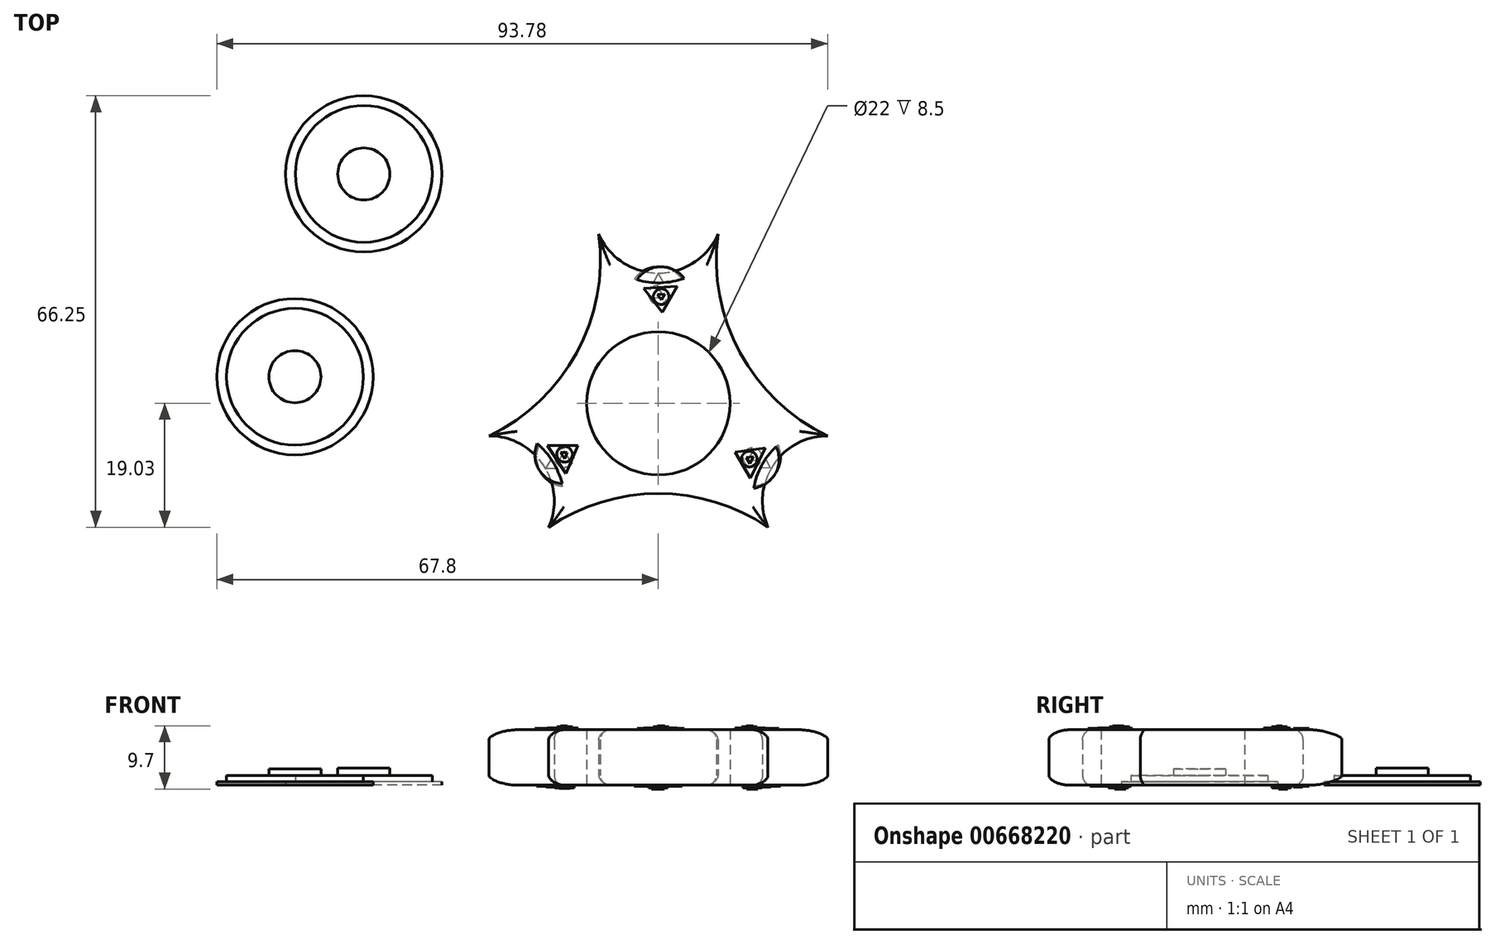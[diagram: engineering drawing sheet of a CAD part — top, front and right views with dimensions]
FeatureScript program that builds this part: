
annotation { "Feature Type Name" : "Feature", "Feature Type Description" : "" }
export const myFeature = defineFeature(function(context is Context, id is Id, definition is map)
    precondition{}
    {
        {
            var Q0;
            Q0=qCreatedBy(makeId("Top.planeOp"),FACE);
            var sketch = newSketch(context, id + "F0", { "sketchPlane" : qUnion([Q0])});
            skCircle(sketch, "E0", {"center": v(0, 0) * mm, "radius": 11 * mm});
            skLineSegment(sketch, "E1", {"start": v(0, 30) * mm, "end": v(0, 0) * mm});
            skLineSegment(sketch, "E2.0", {"start": v(-25.98, 15) * mm, "end": v(25.98, 15) * mm});
            skLineSegment(sketch, "E2.1", {"start": v(25.98, 15) * mm, "end": v(0, -30) * mm});
            skLineSegment(sketch, "E2.2", {"start": v(0, -30) * mm, "end": v(-25.98, 15) * mm});
            skPoint(sketch, "E2.0.midPoint", {"position": v(0, 15) * mm});
            skLineSegment(sketch, "E3", {"start": v(0, 0) * mm, "end": v(25.98, -15) * mm});
            skLineSegment(sketch, "E4", {"start": v(25.98, -15) * mm, "end": v(0, 0) * mm});
            skLineSegment(sketch, "E5", {"start": v(0, 0) * mm, "end": v(-25.98, -15) * mm});
            skLineSegment(sketch, "E6", {"start": v(-25.98, -15) * mm, "end": v(0, 0) * mm});
            skCircle(sketch, "E7", {"center": v(-25.98, -15) * mm, "radius": 10 * mm});
            skCircle(sketch, "E8", {"center": v(25.98, -15) * mm, "radius": 10 * mm});
            skCircle(sketch, "E9", {"center": v(0, 30) * mm, "radius": 10 * mm});
            skArc(sketch, "E10", {"start": v(16.83, -19.02) * mm, "mid": v(0, -13.86) * mm, "end": v(-16.83, -19.03) * mm});
            skArc(sketch, "E11", {"start": v(-25.98, -5) * mm, "mid": v(-12.54, 7.76) * mm, "end": v(-9.15, 25.97) * mm});
            skArc(sketch, "E12", {"start": v(9.15, 25.97) * mm, "mid": v(12.54, 7.76) * mm, "end": v(25.98, -5) * mm});
            skPoint(sketch, "E13.0.midPoint", {"position": v(18.83, -15) * mm});
            skPoint(sketch, "E14.0.midPoint", {"position": v(-18.83, -15) * mm});
            skPoint(sketch, "E15.0.midPoint", {"position": v(7.15, 30) * mm});
            skPoint(sketch, "E16.orphan", {"position": v(7.15, 34.13) * mm});
            skPoint(sketch, "E15.1.start.orphan", {"position": v(7.15, 25.87) * mm});
            skPoint(sketch, "E13.0.end.orphan", {"position": v(18.83, -10.87) * mm});
            skPoint(sketch, "E13.5.end.orphan", {"position": v(18.83, -19.13) * mm});
            skPoint(sketch, "E17.orphan", {"position": v(-18.83, -10.87) * mm});
            skPoint(sketch, "E14.0.end.orphan", {"position": v(-18.83, -19.13) * mm});
            skCircle(sketch, "E18.cCircle", {"center": v(0, 30) * mm, "radius": 7.02 * mm, "construction": true});
            skLineSegment(sketch, "E18.0", {"start": v(0, 37.02) * mm, "end": v(6.08, 33.51) * mm});
            skLineSegment(sketch, "E18.1", {"start": v(6.08, 33.51) * mm, "end": v(6.08, 26.49) * mm});
            skLineSegment(sketch, "E18.2", {"start": v(6.08, 26.49) * mm, "end": v(0, 22.98) * mm});
            skLineSegment(sketch, "E18.3", {"start": v(0, 22.98) * mm, "end": v(-6.08, 26.49) * mm});
            skLineSegment(sketch, "E18.4", {"start": v(-6.08, 26.49) * mm, "end": v(-6.08, 33.51) * mm});
            skLineSegment(sketch, "E18.5", {"start": v(-6.08, 33.51) * mm, "end": v(0, 37.02) * mm});
            skSolve(sketch);
        }
        {
            var Q0;
            Q0=makeQuery(id+"F0.imprint","IMPRINT",FACE,{"disambiguationData":[TD([[makeQuery(id+"F0.imprint","IMPRINT",EDGE,{"derivedFrom":sQuery(id+"F0.wireOp",EDGE,"E15.0")}),1.0]])]});
            var Q1;
            {var subQ0=sQuery(id+"F0.wireOp",EDGE,"E9");var subQ1=sQuery(id+"F0.wireOp",EDGE,"E1");var subQ2=makeQuery(id+"F0.imprint","INTERSECT",VERTEX,{"derivedFrom":[subQ1,subQ0]});Q1=makeQuery(id+"F0.imprint","IMPRINT",FACE,{"disambiguationData":[TD([[makeQuery(id+"F0.imprint","IMPRINT",EDGE,{"disambiguationData":[TD([[subQ2,-1.0]])],"derivedFrom":subQ1}),-1.0]])]});}
            var Q2;
            {var subQ0=sQuery(id+"F0.wireOp",EDGE,"E9");var subQ1=sQuery(id+"F0.wireOp",EDGE,"E1");var subQ2=makeQuery(id+"F0.imprint","INTERSECT",VERTEX,{"derivedFrom":[subQ1,subQ0]});Q2=makeQuery(id+"F0.imprint","IMPRINT",FACE,{"disambiguationData":[TD([[makeQuery(id+"F0.imprint","IMPRINT",EDGE,{"disambiguationData":[TD([[subQ2,-1.0]])],"derivedFrom":subQ1}),1.0]])]});}
            var Q3;
            {var subQ7=sQuery(id+"F0.wireOp",EDGE,"E1");var subQ9=sQuery(id+"F0.wireOp",EDGE,"E0");var subQ11=makeQuery(id+"F0.imprint","INTERSECT",VERTEX,{"derivedFrom":[subQ9,subQ7]});Q3=makeQuery(id+"F0.imprint","IMPRINT",FACE,{"disambiguationData":[TD([[makeQuery(id+"F0.imprint","IMPRINT",EDGE,{"disambiguationData":[TD([[subQ11,1.0]])],"derivedFrom":subQ9}),-1.0]])]});}
            var Q4;
            {var subQ3=sQuery(id+"F0.wireOp",EDGE,"E6");var subQ9=sQuery(id+"F0.wireOp",EDGE,"E0");var subQ11=makeQuery(id+"F0.imprint","INTERSECT",VERTEX,{"derivedFrom":[subQ9,subQ3]});Q4=makeQuery(id+"F0.imprint","IMPRINT",FACE,{"disambiguationData":[TD([[makeQuery(id+"F0.imprint","IMPRINT",EDGE,{"disambiguationData":[TD([[subQ11,1.0]])],"derivedFrom":subQ9}),-1.0]])]});}
            var Q5;
            Q5=makeQuery(id+"F0.imprint","IMPRINT",FACE,{"disambiguationData":[TD([[makeQuery(id+"F0.imprint","IMPRINT",EDGE,{"derivedFrom":sQuery(id+"F0.wireOp",EDGE,"E14.0")}),1.0]])]});
            var Q6;
            {var subQ0=sQuery(id+"F0.wireOp",EDGE,"E11");var subQ1=sQuery(id+"F0.wireOp",EDGE,"E2.2");var subQ2=makeQuery(id+"F0.imprint","INTERSECT",VERTEX,{"derivedFrom":[subQ1,subQ0]});Q6=makeQuery(id+"F0.imprint","IMPRINT",FACE,{"disambiguationData":[TD([[makeQuery(id+"F0.imprint","IMPRINT",EDGE,{"disambiguationData":[TD([[subQ2,1.0]])],"derivedFrom":subQ1}),1.0]])]});}
            var Q7;
            {var subQ0=sQuery(id+"F0.wireOp",EDGE,"E10");var subQ1=sQuery(id+"F0.wireOp",EDGE,"E2.2");var subQ2=makeQuery(id+"F0.imprint","INTERSECT",VERTEX,{"derivedFrom":[subQ1,subQ0]});Q7=makeQuery(id+"F0.imprint","IMPRINT",FACE,{"disambiguationData":[TD([[makeQuery(id+"F0.imprint","IMPRINT",EDGE,{"disambiguationData":[TD([[subQ2,-1.0]])],"derivedFrom":subQ1}),1.0]])]});}
            var Q8;
            {var subQ1=sQuery(id+"F0.wireOp",EDGE,"E0");var subQ8=sQuery(id+"F0.wireOp",EDGE,"E6");var subQ11=makeQuery(id+"F0.imprint","INTERSECT",VERTEX,{"derivedFrom":[subQ1,subQ8]});Q8=makeQuery(id+"F0.imprint","IMPRINT",FACE,{"disambiguationData":[TD([[makeQuery(id+"F0.imprint","IMPRINT",EDGE,{"disambiguationData":[TD([[subQ11,-1.0]])],"derivedFrom":subQ1}),-1.0]])]});}
            var Q9;
            {var subQ0=sQuery(id+"F0.wireOp",EDGE,"E10");var subQ1=sQuery(id+"F0.wireOp",EDGE,"E2.1");var subQ2=makeQuery(id+"F0.imprint","INTERSECT",VERTEX,{"derivedFrom":[subQ1,subQ0]});Q9=makeQuery(id+"F0.imprint","IMPRINT",FACE,{"disambiguationData":[TD([[makeQuery(id+"F0.imprint","IMPRINT",EDGE,{"disambiguationData":[TD([[subQ2,1.0]])],"derivedFrom":subQ1}),1.0]])]});}
            var Q10;
            {var subQ0=sQuery(id+"F0.wireOp",EDGE,"E12");var subQ1=sQuery(id+"F0.wireOp",EDGE,"E2.1");var subQ2=makeQuery(id+"F0.imprint","INTERSECT",VERTEX,{"derivedFrom":[subQ1,subQ0]});Q10=makeQuery(id+"F0.imprint","IMPRINT",FACE,{"disambiguationData":[TD([[makeQuery(id+"F0.imprint","IMPRINT",EDGE,{"disambiguationData":[TD([[subQ2,-1.0]])],"derivedFrom":subQ1}),1.0]])]});}
            var Q11;
            Q11=makeQuery(id+"F0.imprint","IMPRINT",FACE,{"disambiguationData":[TD([[makeQuery(id+"F0.imprint","IMPRINT",EDGE,{"derivedFrom":sQuery(id+"F0.wireOp",EDGE,"E13.0")}),1.0]])]});
            extrude(context, id + "F1", {"entities" : qUnion([Q0, Q1, Q2, Q3, Q4, Q5, Q6, Q7, Q8, Q9, Q10, Q11]), "depth" : 8.5 * mm, "offsetDistance" : 25 * mm});
        }
        {
            var Q0;
            Q0=makeQuery(id+"F1.opExtrude","CAP_FACE",FACE,{"disambiguationData":[OSD([sQuery(id+"F0.wireOp",EDGE,"E0"),sQuery(id+"F0.wireOp",EDGE,"6ecd8433-be9a-4efb-821e-c5c08fbd8d0d.0"),sQuery(id+"F0.wireOp",EDGE,"6ecd8433-be9a-4efb-821e-c5c08fbd8d0d.1"),sQuery(id+"F0.wireOp",EDGE,"6ecd8433-be9a-4efb-821e-c5c08fbd8d0d.2"),sQuery(id+"F0.wireOp",EDGE,"6ecd8433-be9a-4efb-821e-c5c08fbd8d0d.3"),sQuery(id+"F0.wireOp",EDGE,"6ecd8433-be9a-4efb-821e-c5c08fbd8d0d.4"),sQuery(id+"F0.wireOp",EDGE,"6ecd8433-be9a-4efb-821e-c5c08fbd8d0d.5"),sQuery(id+"F0.wireOp",EDGE,"1ad9032f-628d-491e-8cbe-ab9449ec9861.0"),sQuery(id+"F0.wireOp",EDGE,"1ad9032f-628d-491e-8cbe-ab9449ec9861.1"),sQuery(id+"F0.wireOp",EDGE,"1ad9032f-628d-491e-8cbe-ab9449ec9861.2"),sQuery(id+"F0.wireOp",EDGE,"1ad9032f-628d-491e-8cbe-ab9449ec9861.3"),sQuery(id+"F0.wireOp",EDGE,"1ad9032f-628d-491e-8cbe-ab9449ec9861.4"),sQuery(id+"F0.wireOp",EDGE,"1ad9032f-628d-491e-8cbe-ab9449ec9861.5"),sQuery(id+"F0.wireOp",EDGE,"2cabaf14-cadd-46fb-af4e-32f49395d764.0"),sQuery(id+"F0.wireOp",EDGE,"2cabaf14-cadd-46fb-af4e-32f49395d764.1"),sQuery(id+"F0.wireOp",EDGE,"2cabaf14-cadd-46fb-af4e-32f49395d764.2"),sQuery(id+"F0.wireOp",EDGE,"2cabaf14-cadd-46fb-af4e-32f49395d764.3"),sQuery(id+"F0.wireOp",EDGE,"2cabaf14-cadd-46fb-af4e-32f49395d764.4"),sQuery(id+"F0.wireOp",EDGE,"2cabaf14-cadd-46fb-af4e-32f49395d764.5"),sQuery(id+"F0.wireOp",EDGE,"E7"),sQuery(id+"F0.wireOp",EDGE,"E8"),sQuery(id+"F0.wireOp",EDGE,"E9"),sQuery(id+"F0.wireOp",EDGE,"E10"),sQuery(id+"F0.wireOp",EDGE,"E11"),sQuery(id+"F0.wireOp",EDGE,"E12")])],"isStart":false});
            var sketch = newSketch(context, id + "F2", { "sketchPlane" : qUnion([Q0])});
            skCircle(sketch, "E19", {"center": v(0, 16.47) * mm, "radius": 3.47 * mm});
            skCircle(sketch, "E20", {"center": v(-14.27, -8.24) * mm, "radius": 3.48 * mm});
            skCircle(sketch, "E21", {"center": v(14.27, -8.24) * mm, "radius": 3.47 * mm});
            skSolve(sketch);
        }
        {
            var Q0;
            Q0=makeQuery(id+"F1.opExtrude","CAP_EDGE",EDGE,{"disambiguationData":[OSD([sQuery(id+"F0.wireOp",EDGE,"E11")])],"isStart":false});
            var Q1;
            Q1=makeQuery(id+"F1.opExtrude","CAP_EDGE",EDGE,{"disambiguationData":[OSD([sQuery(id+"F0.wireOp",EDGE,"E9")])],"isStart":false});
            var Q2;
            Q2=makeQuery(id+"F1.opExtrude","CAP_EDGE",EDGE,{"disambiguationData":[OSD([sQuery(id+"F0.wireOp",EDGE,"E12")])],"isStart":false});
            var Q3;
            Q3=makeQuery(id+"F1.opExtrude","CAP_EDGE",EDGE,{"disambiguationData":[OSD([sQuery(id+"F0.wireOp",EDGE,"E10")])],"isStart":false});
            var Q4;
            Q4=makeQuery(id+"F1.opExtrude","CAP_EDGE",EDGE,{"disambiguationData":[OSD([sQuery(id+"F0.wireOp",EDGE,"E7")])],"isStart":false});
            var Q5;
            Q5=makeQuery(id+"F1.opExtrude","CAP_EDGE",EDGE,{"disambiguationData":[OSD([sQuery(id+"F0.wireOp",EDGE,"E8")])],"isStart":false});
            var Q6;
            Q6=makeQuery(id+"FblKMbQ7xXgYiAB_1.boolean.opBoolean","COPY",EDGE,{"derivedFrom":makeQuery(id+"FblKMbQ7xXgYiAB_1.opExtrude","CAP_EDGE",EDGE,{"disambiguationData":[OSD([sQuery(id+"F2.wireOp",EDGE,"E21")])],"isStart":true})});
            var Q7;
            Q7=makeQuery(id+"FblKMbQ7xXgYiAB_1.boolean.opBoolean","COPY",EDGE,{"derivedFrom":makeQuery(id+"FblKMbQ7xXgYiAB_1.opExtrude","CAP_EDGE",EDGE,{"disambiguationData":[OSD([sQuery(id+"F2.wireOp",EDGE,"E20")])],"isStart":true})});
            var Q8;
            Q8=makeQuery(id+"FblKMbQ7xXgYiAB_1.boolean.opBoolean","COPY",EDGE,{"derivedFrom":makeQuery(id+"FblKMbQ7xXgYiAB_1.opExtrude","CAP_EDGE",EDGE,{"disambiguationData":[OSD([sQuery(id+"F2.wireOp",EDGE,"E19")])],"isStart":true})});
            var Q9;
            Q9=makeQuery(id+"F1.opExtrude","CAP_EDGE",EDGE,{"disambiguationData":[OSD([sQuery(id+"F0.wireOp",EDGE,"E10")])],"isStart":true});
            var Q10;
            Q10=makeQuery(id+"F1.opExtrude","CAP_EDGE",EDGE,{"disambiguationData":[OSD([sQuery(id+"F0.wireOp",EDGE,"E11")])],"isStart":true});
            var Q11;
            Q11=makeQuery(id+"F1.opExtrude","CAP_EDGE",EDGE,{"disambiguationData":[OSD([sQuery(id+"F0.wireOp",EDGE,"E9")])],"isStart":true});
            var Q12;
            Q12=makeQuery(id+"F1.opExtrude","CAP_EDGE",EDGE,{"disambiguationData":[OSD([sQuery(id+"F0.wireOp",EDGE,"E12")])],"isStart":true});
            var Q13;
            Q13=makeQuery(id+"F1.opExtrude","CAP_EDGE",EDGE,{"disambiguationData":[OSD([sQuery(id+"F0.wireOp",EDGE,"E8")])],"isStart":true});
            var Q14;
            Q14=makeQuery(id+"F1.opExtrude","CAP_EDGE",EDGE,{"disambiguationData":[OSD([sQuery(id+"F0.wireOp",EDGE,"E7")])],"isStart":true});
            var Q15;
            Q15=makeQuery(id+"FblKMbQ7xXgYiAB_1.boolean.opBoolean","INTERSECT",EDGE,{"derivedFrom":[makeQuery(id+"F1.opExtrude","CAP_FACE",FACE,{"disambiguationData":[OSD([sQuery(id+"F0.wireOp",EDGE,"E0"),sQuery(id+"F0.wireOp",EDGE,"6ecd8433-be9a-4efb-821e-c5c08fbd8d0d.0"),sQuery(id+"F0.wireOp",EDGE,"6ecd8433-be9a-4efb-821e-c5c08fbd8d0d.1"),sQuery(id+"F0.wireOp",EDGE,"6ecd8433-be9a-4efb-821e-c5c08fbd8d0d.2"),sQuery(id+"F0.wireOp",EDGE,"6ecd8433-be9a-4efb-821e-c5c08fbd8d0d.3"),sQuery(id+"F0.wireOp",EDGE,"6ecd8433-be9a-4efb-821e-c5c08fbd8d0d.4"),sQuery(id+"F0.wireOp",EDGE,"6ecd8433-be9a-4efb-821e-c5c08fbd8d0d.5"),sQuery(id+"F0.wireOp",EDGE,"1ad9032f-628d-491e-8cbe-ab9449ec9861.0"),sQuery(id+"F0.wireOp",EDGE,"1ad9032f-628d-491e-8cbe-ab9449ec9861.1"),sQuery(id+"F0.wireOp",EDGE,"1ad9032f-628d-491e-8cbe-ab9449ec9861.2"),sQuery(id+"F0.wireOp",EDGE,"1ad9032f-628d-491e-8cbe-ab9449ec9861.3"),sQuery(id+"F0.wireOp",EDGE,"1ad9032f-628d-491e-8cbe-ab9449ec9861.4"),sQuery(id+"F0.wireOp",EDGE,"1ad9032f-628d-491e-8cbe-ab9449ec9861.5"),sQuery(id+"F0.wireOp",EDGE,"2cabaf14-cadd-46fb-af4e-32f49395d764.0"),sQuery(id+"F0.wireOp",EDGE,"2cabaf14-cadd-46fb-af4e-32f49395d764.1"),sQuery(id+"F0.wireOp",EDGE,"2cabaf14-cadd-46fb-af4e-32f49395d764.2"),sQuery(id+"F0.wireOp",EDGE,"2cabaf14-cadd-46fb-af4e-32f49395d764.3"),sQuery(id+"F0.wireOp",EDGE,"2cabaf14-cadd-46fb-af4e-32f49395d764.4"),sQuery(id+"F0.wireOp",EDGE,"2cabaf14-cadd-46fb-af4e-32f49395d764.5"),sQuery(id+"F0.wireOp",EDGE,"E7"),sQuery(id+"F0.wireOp",EDGE,"E8"),sQuery(id+"F0.wireOp",EDGE,"E9"),sQuery(id+"F0.wireOp",EDGE,"E10"),sQuery(id+"F0.wireOp",EDGE,"E11"),sQuery(id+"F0.wireOp",EDGE,"E12")])],"isStart":true}),makeQuery(id+"FblKMbQ7xXgYiAB_1.opExtrude","SWEPT_FACE",FACE,{"disambiguationData":[OSD([sQuery(id+"F2.wireOp",EDGE,"E20")])]})]});
            var Q16;
            Q16=makeQuery(id+"FblKMbQ7xXgYiAB_1.boolean.opBoolean","INTERSECT",EDGE,{"derivedFrom":[makeQuery(id+"F1.opExtrude","CAP_FACE",FACE,{"disambiguationData":[OSD([sQuery(id+"F0.wireOp",EDGE,"E0"),sQuery(id+"F0.wireOp",EDGE,"6ecd8433-be9a-4efb-821e-c5c08fbd8d0d.0"),sQuery(id+"F0.wireOp",EDGE,"6ecd8433-be9a-4efb-821e-c5c08fbd8d0d.1"),sQuery(id+"F0.wireOp",EDGE,"6ecd8433-be9a-4efb-821e-c5c08fbd8d0d.2"),sQuery(id+"F0.wireOp",EDGE,"6ecd8433-be9a-4efb-821e-c5c08fbd8d0d.3"),sQuery(id+"F0.wireOp",EDGE,"6ecd8433-be9a-4efb-821e-c5c08fbd8d0d.4"),sQuery(id+"F0.wireOp",EDGE,"6ecd8433-be9a-4efb-821e-c5c08fbd8d0d.5"),sQuery(id+"F0.wireOp",EDGE,"1ad9032f-628d-491e-8cbe-ab9449ec9861.0"),sQuery(id+"F0.wireOp",EDGE,"1ad9032f-628d-491e-8cbe-ab9449ec9861.1"),sQuery(id+"F0.wireOp",EDGE,"1ad9032f-628d-491e-8cbe-ab9449ec9861.2"),sQuery(id+"F0.wireOp",EDGE,"1ad9032f-628d-491e-8cbe-ab9449ec9861.3"),sQuery(id+"F0.wireOp",EDGE,"1ad9032f-628d-491e-8cbe-ab9449ec9861.4"),sQuery(id+"F0.wireOp",EDGE,"1ad9032f-628d-491e-8cbe-ab9449ec9861.5"),sQuery(id+"F0.wireOp",EDGE,"2cabaf14-cadd-46fb-af4e-32f49395d764.0"),sQuery(id+"F0.wireOp",EDGE,"2cabaf14-cadd-46fb-af4e-32f49395d764.1"),sQuery(id+"F0.wireOp",EDGE,"2cabaf14-cadd-46fb-af4e-32f49395d764.2"),sQuery(id+"F0.wireOp",EDGE,"2cabaf14-cadd-46fb-af4e-32f49395d764.3"),sQuery(id+"F0.wireOp",EDGE,"2cabaf14-cadd-46fb-af4e-32f49395d764.4"),sQuery(id+"F0.wireOp",EDGE,"2cabaf14-cadd-46fb-af4e-32f49395d764.5"),sQuery(id+"F0.wireOp",EDGE,"E7"),sQuery(id+"F0.wireOp",EDGE,"E8"),sQuery(id+"F0.wireOp",EDGE,"E9"),sQuery(id+"F0.wireOp",EDGE,"E10"),sQuery(id+"F0.wireOp",EDGE,"E11"),sQuery(id+"F0.wireOp",EDGE,"E12")])],"isStart":true}),makeQuery(id+"FblKMbQ7xXgYiAB_1.opExtrude","SWEPT_FACE",FACE,{"disambiguationData":[OSD([sQuery(id+"F2.wireOp",EDGE,"E19")])]})]});
            var Q17;
            Q17=makeQuery(id+"FblKMbQ7xXgYiAB_1.boolean.opBoolean","INTERSECT",EDGE,{"derivedFrom":[makeQuery(id+"F1.opExtrude","CAP_FACE",FACE,{"disambiguationData":[OSD([sQuery(id+"F0.wireOp",EDGE,"E0"),sQuery(id+"F0.wireOp",EDGE,"6ecd8433-be9a-4efb-821e-c5c08fbd8d0d.0"),sQuery(id+"F0.wireOp",EDGE,"6ecd8433-be9a-4efb-821e-c5c08fbd8d0d.1"),sQuery(id+"F0.wireOp",EDGE,"6ecd8433-be9a-4efb-821e-c5c08fbd8d0d.2"),sQuery(id+"F0.wireOp",EDGE,"6ecd8433-be9a-4efb-821e-c5c08fbd8d0d.3"),sQuery(id+"F0.wireOp",EDGE,"6ecd8433-be9a-4efb-821e-c5c08fbd8d0d.4"),sQuery(id+"F0.wireOp",EDGE,"6ecd8433-be9a-4efb-821e-c5c08fbd8d0d.5"),sQuery(id+"F0.wireOp",EDGE,"1ad9032f-628d-491e-8cbe-ab9449ec9861.0"),sQuery(id+"F0.wireOp",EDGE,"1ad9032f-628d-491e-8cbe-ab9449ec9861.1"),sQuery(id+"F0.wireOp",EDGE,"1ad9032f-628d-491e-8cbe-ab9449ec9861.2"),sQuery(id+"F0.wireOp",EDGE,"1ad9032f-628d-491e-8cbe-ab9449ec9861.3"),sQuery(id+"F0.wireOp",EDGE,"1ad9032f-628d-491e-8cbe-ab9449ec9861.4"),sQuery(id+"F0.wireOp",EDGE,"1ad9032f-628d-491e-8cbe-ab9449ec9861.5"),sQuery(id+"F0.wireOp",EDGE,"2cabaf14-cadd-46fb-af4e-32f49395d764.0"),sQuery(id+"F0.wireOp",EDGE,"2cabaf14-cadd-46fb-af4e-32f49395d764.1"),sQuery(id+"F0.wireOp",EDGE,"2cabaf14-cadd-46fb-af4e-32f49395d764.2"),sQuery(id+"F0.wireOp",EDGE,"2cabaf14-cadd-46fb-af4e-32f49395d764.3"),sQuery(id+"F0.wireOp",EDGE,"2cabaf14-cadd-46fb-af4e-32f49395d764.4"),sQuery(id+"F0.wireOp",EDGE,"2cabaf14-cadd-46fb-af4e-32f49395d764.5"),sQuery(id+"F0.wireOp",EDGE,"E7"),sQuery(id+"F0.wireOp",EDGE,"E8"),sQuery(id+"F0.wireOp",EDGE,"E9"),sQuery(id+"F0.wireOp",EDGE,"E10"),sQuery(id+"F0.wireOp",EDGE,"E11"),sQuery(id+"F0.wireOp",EDGE,"E12")])],"isStart":true}),makeQuery(id+"FblKMbQ7xXgYiAB_1.opExtrude","SWEPT_FACE",FACE,{"disambiguationData":[OSD([sQuery(id+"F2.wireOp",EDGE,"E21")])]})]});
            fillet(context, id + "F3", {"entities" : qUnion([Q0, Q1, Q2, Q3, Q4, Q5, Q6, Q7, Q8, Q9, Q10, Q11, Q12, Q13, Q14, Q15, Q16, Q17]), "radius" : 1.5 * mm, "tangentPropagation" : true, "allowEdgeOverflow" : false});
        }
        {
            var Q0;
            Q0=makeQuery(id+"F1.opExtrude","CAP_FACE",FACE,{"disambiguationData":[OSD([sQuery(id+"F0.wireOp",EDGE,"E0"),sQuery(id+"F0.wireOp",EDGE,"E7"),sQuery(id+"F0.wireOp",EDGE,"E8"),sQuery(id+"F0.wireOp",EDGE,"E9"),sQuery(id+"F0.wireOp",EDGE,"E10"),sQuery(id+"F0.wireOp",EDGE,"E11"),sQuery(id+"F0.wireOp",EDGE,"E12"),sQuery(id+"F0.wireOp",EDGE,"E13.0"),sQuery(id+"F0.wireOp",EDGE,"E13.1"),sQuery(id+"F0.wireOp",EDGE,"E13.2"),sQuery(id+"F0.wireOp",EDGE,"E13.3"),sQuery(id+"F0.wireOp",EDGE,"E13.4"),sQuery(id+"F0.wireOp",EDGE,"E13.5"),sQuery(id+"F0.wireOp",EDGE,"E14.0"),sQuery(id+"F0.wireOp",EDGE,"E14.1"),sQuery(id+"F0.wireOp",EDGE,"E14.2"),sQuery(id+"F0.wireOp",EDGE,"E14.3"),sQuery(id+"F0.wireOp",EDGE,"E14.4"),sQuery(id+"F0.wireOp",EDGE,"E14.5"),sQuery(id+"F0.wireOp",EDGE,"E15.0"),sQuery(id+"F0.wireOp",EDGE,"E15.1"),sQuery(id+"F0.wireOp",EDGE,"E15.2"),sQuery(id+"F0.wireOp",EDGE,"E15.3"),sQuery(id+"F0.wireOp",EDGE,"E15.4"),sQuery(id+"F0.wireOp",EDGE,"E15.5")])],"isStart":false});
            var sketch = newSketch(context, id + "F4", { "sketchPlane" : qUnion([Q0])});
            skPoint(sketch, "E22.0.start.orphan", {"position": v(18.83, -15) * mm});
            skCircle(sketch, "E23", {"center": v(-14.5, -7.9) * mm, "radius": 4.45 * mm});
            skLineSegment(sketch, "E24", {"start": v(-12.36, -6.47) * mm, "end": v(-17.04, -6.47) * mm});
            skLineSegment(sketch, "E25", {"start": v(-17.04, -6.47) * mm, "end": v(-15.6, -8.62) * mm});
            skLineSegment(sketch, "E26.MirrorCS", {"start": v(-12.36, -6.47) * mm, "end": v(-14.18, -10.78) * mm});
            skLineSegment(sketch, "E27.MirrorCS", {"start": v(-14.18, -10.78) * mm, "end": v(-15.6, -8.62) * mm});
            skCircle(sketch, "E28.1.0", {"center": v(14.08, -8.61) * mm, "radius": 4.45 * mm});
            skCircle(sketch, "E28.2.0", {"center": v(0.42, 16.5) * mm, "radius": 4.45 * mm});
            skPoint(sketch, "E28.center", {"position": v(0, 0) * mm});
            skLineSegment(sketch, "E29.1.0", {"start": v(11.78, -7.47) * mm, "end": v(16.42, -6.89) * mm});
            skLineSegment(sketch, "E29.1.1", {"start": v(14.12, -11.52) * mm, "end": v(15.27, -9.2) * mm});
            skLineSegment(sketch, "E29.1.2", {"start": v(16.42, -6.89) * mm, "end": v(15.27, -9.2) * mm});
            skLineSegment(sketch, "E29.1.3", {"start": v(11.78, -7.47) * mm, "end": v(14.12, -11.52) * mm});
            skLineSegment(sketch, "E29.2.0", {"start": v(0.58, 13.94) * mm, "end": v(-2.25, 17.67) * mm});
            skLineSegment(sketch, "E29.2.1", {"start": v(2.92, 17.99) * mm, "end": v(0.33, 17.83) * mm});
            skLineSegment(sketch, "E29.2.2", {"start": v(-2.25, 17.67) * mm, "end": v(0.33, 17.83) * mm});
            skLineSegment(sketch, "E29.2.3", {"start": v(0.58, 13.94) * mm, "end": v(2.92, 17.99) * mm});
            skSolve(sketch);
        }
        {
            var Q0;
            Q0=makeQuery(id+"F4.imprint","IMPRINT",FACE,{"disambiguationData":[TD([[makeQuery(id+"F4.imprint","IMPRINT",EDGE,{"derivedFrom":sQuery(id+"F4.wireOp",EDGE,"E29.1.0")}),-1.0]])]});
            var Q1;
            Q1=makeQuery(id+"F4.imprint","IMPRINT",FACE,{"disambiguationData":[TD([[makeQuery(id+"F4.imprint","IMPRINT",EDGE,{"derivedFrom":sQuery(id+"F4.wireOp",EDGE,"E24")}),1.0]])]});
            var Q2;
            Q2=makeQuery(id+"F4.imprint","IMPRINT",FACE,{"disambiguationData":[TD([[makeQuery(id+"F4.imprint","IMPRINT",EDGE,{"derivedFrom":sQuery(id+"F4.wireOp",EDGE,"E29.2.0")}),-1.0]])]});
            extrude(context, id + "F5", {"entities" : qUnion([Q0, Q1, Q2]), "operationType" : NewBodyOperationType.ADD, "depth" : .3 * mm, "offsetDistance" : 25 * mm});
        }
        {
            var Q0;
            Q0=makeQuery(id+"F4.imprint","IMPRINT",FACE,{"disambiguationData":[TD([[makeQuery(id+"F4.imprint","IMPRINT",EDGE,{"derivedFrom":sQuery(id+"F4.wireOp",EDGE,"E28.1.0")}),1.0]])]});
            var Q1;
            Q1=makeQuery(id+"F4.imprint","IMPRINT",FACE,{"disambiguationData":[TD([[makeQuery(id+"F4.imprint","IMPRINT",EDGE,{"derivedFrom":sQuery(id+"F4.wireOp",EDGE,"E23")}),1.0]])]});
            var Q2;
            Q2=makeQuery(id+"F4.imprint","IMPRINT",FACE,{"disambiguationData":[TD([[makeQuery(id+"F4.imprint","IMPRINT",EDGE,{"derivedFrom":sQuery(id+"F4.wireOp",EDGE,"E28.2.0")}),1.0]])]});
            extrude(context, id + "F6", {"entities" : qUnion([Q0, Q1, Q2]), "operationType" : NewBodyOperationType.ADD, "depth" : .2 * mm, "offsetDistance" : 25 * mm});
        }
        {
            var Q0;
            Q0=makeQuery(id+"F5.opExtrude","CAP_FACE",FACE,{"disambiguationData":[OSD([sQuery(id+"F4.wireOp",EDGE,"E24"),sQuery(id+"F4.wireOp",EDGE,"E25"),sQuery(id+"F4.wireOp",EDGE,"E26.MirrorCS"),sQuery(id+"F4.wireOp",EDGE,"E27.MirrorCS")])],"isStart":false});
            var sketch = newSketch(context, id + "F7", { "sketchPlane" : qUnion([Q0])});
            skLineSegment(sketch, "E30", {"start": v(-12.36, -6.47) * mm, "end": v(-15.6, -8.62) * mm});
            skCircle(sketch, "E31", {"center": v(-14.4, -7.82) * mm, "radius": 1.2 * mm});
            skLineSegment(sketch, "E32", {"start": v(-13.98, -7.55) * mm, "end": v(-15.03, -7.55) * mm});
            skLineSegment(sketch, "E33", {"start": v(-15.03, -7.55) * mm, "end": v(-14.71, -8.03) * mm});
            skLineSegment(sketch, "E34.MirrorCS", {"start": v(-17.06, -9.6) * mm, "end": v(-13.82, -7.44) * mm});
            skLineSegment(sketch, "E35.MirrorCS", {"start": v(-14.4, -8.51) * mm, "end": v(-14.71, -8.03) * mm});
            skLineSegment(sketch, "E36.MirrorCS", {"start": v(-13.98, -7.55) * mm, "end": v(-14.4, -8.51) * mm});
            skLineSegment(sketch, "E37.1.0", {"start": v(14.05, -9.25) * mm, "end": v(14.31, -8.73) * mm});
            skLineSegment(sketch, "E37.1.1", {"start": v(14.57, -8.2) * mm, "end": v(14.31, -8.73) * mm});
            skLineSegment(sketch, "E37.1.2", {"start": v(13.53, -8.34) * mm, "end": v(14.57, -8.2) * mm});
            skCircle(sketch, "E37.1.3", {"center": v(13.97, -8.56) * mm, "radius": 1.2 * mm});
            skLineSegment(sketch, "E37.1.4", {"start": v(13.53, -8.34) * mm, "end": v(14.05, -9.25) * mm});
            skLineSegment(sketch, "E37.2.0", {"start": v(0.98, 16.8) * mm, "end": v(0.4, 16.76) * mm});
            skLineSegment(sketch, "E37.2.1", {"start": v(-0.18, 16.72) * mm, "end": v(0.4, 16.76) * mm});
            skLineSegment(sketch, "E37.2.2", {"start": v(0.46, 15.88) * mm, "end": v(-0.18, 16.72) * mm});
            skCircle(sketch, "E37.2.3", {"center": v(0.43, 16.38) * mm, "radius": 1.2 * mm});
            skLineSegment(sketch, "E37.2.4", {"start": v(0.46, 15.88) * mm, "end": v(0.98, 16.8) * mm});
            skPoint(sketch, "E37.center", {"position": v(0, 0) * mm});
            skSolve(sketch);
        }
        {
            var Q0;
            Q0 = qSketchRegion(id + "F7", true);
            extrude(context, id + "F8", {"entities" : qUnion([Q0]), "operationType" : NewBodyOperationType.ADD, "depth" : .2 * mm, "offsetDistance" : 25 * mm});
        }
        {
            var Q0;
            {var subQ2=sQuery(id+"F7.wireOp",EDGE,"E35.MirrorCS");Q0=makeQuery(id+"F7.imprint","IMPRINT",FACE,{"disambiguationData":[TD([[makeQuery(id+"F7.imprint","IMPRINT",EDGE,{"derivedFrom":subQ2}),-1.0]])]});}
            var Q1;
            {var subQ0=sQuery(id+"F7.wireOp",EDGE,"E32");Q1=makeQuery(id+"F7.imprint","IMPRINT",FACE,{"disambiguationData":[TD([[makeQuery(id+"F7.imprint","IMPRINT",EDGE,{"derivedFrom":subQ0}),1.0]])]});}
            extrude(context, id + "F9", {"entities" : qUnion([Q0, Q1]), "operationType" : NewBodyOperationType.ADD, "depth" : .3 * mm, "offsetDistance" : 25 * mm});
        }
        {
            var Q0;
            Q0=makeQuery(id+"F7.imprint","IMPRINT",FACE,{"disambiguationData":[TD([[makeQuery(id+"F7.imprint","IMPRINT",EDGE,{"derivedFrom":sQuery(id+"F7.wireOp",EDGE,"E37.1.0")}),1.0]])]});
            extrude(context, id + "F10", {"entities" : qUnion([Q0]), "operationType" : NewBodyOperationType.ADD, "depth" : .3 * mm, "offsetDistance" : 25 * mm});
        }
        {
            var Q0;
            Q0=makeQuery(id+"F7.imprint","IMPRINT",FACE,{"disambiguationData":[TD([[makeQuery(id+"F7.imprint","IMPRINT",EDGE,{"derivedFrom":sQuery(id+"F7.wireOp",EDGE,"E37.2.0")}),1.0]])]});
            extrude(context, id + "F11", {"entities" : qUnion([Q0]), "operationType" : NewBodyOperationType.ADD, "depth" : .3 * mm, "offsetDistance" : 25 * mm});
        }
        {
            var Q0;
            Q0=makeQuery(id+"F1.opExtrude","CAP_FACE",FACE,{"disambiguationData":[OSD([sQuery(id+"F0.wireOp",EDGE,"E0"),sQuery(id+"F0.wireOp",EDGE,"E7"),sQuery(id+"F0.wireOp",EDGE,"E8"),sQuery(id+"F0.wireOp",EDGE,"E9"),sQuery(id+"F0.wireOp",EDGE,"E10"),sQuery(id+"F0.wireOp",EDGE,"E11"),sQuery(id+"F0.wireOp",EDGE,"E12"),sQuery(id+"F0.wireOp",EDGE,"E13.0"),sQuery(id+"F0.wireOp",EDGE,"E13.1"),sQuery(id+"F0.wireOp",EDGE,"E13.2"),sQuery(id+"F0.wireOp",EDGE,"E13.3"),sQuery(id+"F0.wireOp",EDGE,"E13.4"),sQuery(id+"F0.wireOp",EDGE,"E13.5"),sQuery(id+"F0.wireOp",EDGE,"E14.0"),sQuery(id+"F0.wireOp",EDGE,"E14.1"),sQuery(id+"F0.wireOp",EDGE,"E14.2"),sQuery(id+"F0.wireOp",EDGE,"E14.3"),sQuery(id+"F0.wireOp",EDGE,"E14.4"),sQuery(id+"F0.wireOp",EDGE,"E14.5"),sQuery(id+"F0.wireOp",EDGE,"E15.0"),sQuery(id+"F0.wireOp",EDGE,"E15.1"),sQuery(id+"F0.wireOp",EDGE,"E15.2"),sQuery(id+"F0.wireOp",EDGE,"E15.3"),sQuery(id+"F0.wireOp",EDGE,"E15.4"),sQuery(id+"F0.wireOp",EDGE,"E15.5")])],"isStart":true});
            var sketch = newSketch(context, id + "F12", { "sketchPlane" : qUnion([Q0])});
            skLineSegment(sketch, "E38", {"start": v(-9.49, 5.57) * mm, "end": v(-18.83, 10.87) * mm});
            skCircle(sketch, "E39", {"center": v(-14.16, 8.22) * mm, "radius": 4.56 * mm});
            skLineSegment(sketch, "E40", {"start": v(-17.26, 9.98) * mm, "end": v(-14.16, 4.85) * mm});
            skLineSegment(sketch, "E41", {"start": v(-14.16, 4.85) * mm, "end": v(-12.71, 7.4) * mm});
            skLineSegment(sketch, "E42.MirrorCS", {"start": v(-15.94, 9.23) * mm, "end": v(-6.6, 3.93) * mm});
            skLineSegment(sketch, "E43.MirrorCS", {"start": v(-17.26, 9.98) * mm, "end": v(-11.27, 9.95) * mm});
            skLineSegment(sketch, "E44.MirrorCS", {"start": v(-11.27, 9.95) * mm, "end": v(-12.71, 7.4) * mm});
            skCircle(sketch, "E45", {"center": v(-14.4, 8.36) * mm, "radius": 1.45 * mm});
            skLineSegment(sketch, "E46", {"start": v(-15.23, 8.83) * mm, "end": v(-14.5, 7.3) * mm});
            skLineSegment(sketch, "E47", {"start": v(-14.5, 7.3) * mm, "end": v(-14.03, 8.14) * mm});
            skLineSegment(sketch, "E48.MirrorCS", {"start": v(-15.23, 8.83) * mm, "end": v(-13.54, 9) * mm});
            skLineSegment(sketch, "E49.MirrorCS", {"start": v(-13.54, 9) * mm, "end": v(-14.03, 8.14) * mm});
            skLineSegment(sketch, "E50.1.0", {"start": v(-0.01, -19.94) * mm, "end": v(2.88, -14.69) * mm});
            skLineSegment(sketch, "E50.1.1", {"start": v(2.88, -14.69) * mm, "end": v(-0.05, -14.71) * mm});
            skLineSegment(sketch, "E50.1.2", {"start": v(-1.02, -16.23) * mm, "end": v(-0.04, -16.22) * mm});
            skLineSegment(sketch, "E50.1.3", {"start": v(-0.03, -17.6) * mm, "end": v(-1.02, -16.23) * mm});
            skLineSegment(sketch, "E50.1.4", {"start": v(-0.01, -19.94) * mm, "end": v(-2.98, -14.73) * mm});
            skLineSegment(sketch, "E50.1.5", {"start": v(-0.03, -17.6) * mm, "end": v(0.94, -16.21) * mm});
            skLineSegment(sketch, "E50.1.6", {"start": v(0.94, -16.21) * mm, "end": v(-0.04, -16.22) * mm});
            skCircle(sketch, "E50.1.7", {"center": v(-0.04, -16.66) * mm, "radius": 1.45 * mm});
            skLineSegment(sketch, "E50.1.8", {"start": v(-2.98, -14.73) * mm, "end": v(-0.05, -14.71) * mm});
            skCircle(sketch, "E50.1.9", {"center": v(-0.04, -16.37) * mm, "radius": 4.56 * mm});
            skLineSegment(sketch, "E50.2.0", {"start": v(17.27, 9.96) * mm, "end": v(11.28, 9.83) * mm});
            skLineSegment(sketch, "E50.2.1", {"start": v(11.28, 9.83) * mm, "end": v(12.77, 7.31) * mm});
            skLineSegment(sketch, "E50.2.2", {"start": v(14.56, 7.23) * mm, "end": v(14.07, 8.07) * mm});
            skLineSegment(sketch, "E50.2.3", {"start": v(15.26, 8.77) * mm, "end": v(14.56, 7.23) * mm});
            skLineSegment(sketch, "E50.2.4", {"start": v(17.27, 9.96) * mm, "end": v(14.25, 4.79) * mm});
            skLineSegment(sketch, "E50.2.5", {"start": v(15.26, 8.77) * mm, "end": v(13.57, 8.92) * mm});
            skLineSegment(sketch, "E50.2.6", {"start": v(13.57, 8.92) * mm, "end": v(14.07, 8.07) * mm});
            skCircle(sketch, "E50.2.7", {"center": v(14.45, 8.3) * mm, "radius": 1.45 * mm});
            skLineSegment(sketch, "E50.2.8", {"start": v(14.25, 4.79) * mm, "end": v(12.77, 7.31) * mm});
            skCircle(sketch, "E50.2.9", {"center": v(14.2, 8.15) * mm, "radius": 4.56 * mm});
            skPoint(sketch, "E50.center", {"position": v(0, 0) * mm});
            skSolve(sketch);
        }
        {
            var Q0;
            {var subQ0=sQuery(id+"F12.wireOp",EDGE,"E43.MirrorCS");Q0=makeQuery(id+"F12.imprint","IMPRINT",FACE,{"disambiguationData":[TD([[makeQuery(id+"F12.imprint","IMPRINT",EDGE,{"derivedFrom":subQ0}),1.0]])]});}
            var Q1;
            {var subQ4=sQuery(id+"F12.wireOp",EDGE,"E40");Q1=makeQuery(id+"F12.imprint","IMPRINT",FACE,{"disambiguationData":[TD([[makeQuery(id+"F12.imprint","IMPRINT",EDGE,{"derivedFrom":subQ4}),-1.0]])]});}
            extrude(context, id + "F13", {"entities" : qUnion([Q0, Q1]), "operationType" : NewBodyOperationType.ADD, "depth" : .2 * mm, "offsetDistance" : 25 * mm});
        }
        {
            var Q0;
            {var subQ3=sQuery(id+"F12.wireOp",EDGE,"E43.MirrorCS");Q0=makeQuery(id+"F12.imprint","IMPRINT",FACE,{"disambiguationData":[TD([[makeQuery(id+"F12.imprint","IMPRINT",EDGE,{"derivedFrom":subQ3}),-1.0]])]});}
            var Q1;
            {var subQ0=sQuery(id+"F12.wireOp",EDGE,"E40");Q1=makeQuery(id+"F12.imprint","IMPRINT",FACE,{"disambiguationData":[TD([[makeQuery(id+"F12.imprint","IMPRINT",EDGE,{"derivedFrom":subQ0}),1.0]])]});}
            extrude(context, id + "F14", {"entities" : qUnion([Q0, Q1]), "operationType" : NewBodyOperationType.ADD, "depth" : .3 * mm, "offsetDistance" : 25 * mm});
        }
        {
            var Q0;
            {var subQ4=sQuery(id+"F12.wireOp",EDGE,"E46");Q0=makeQuery(id+"F12.imprint","IMPRINT",FACE,{"disambiguationData":[TD([[makeQuery(id+"F12.imprint","IMPRINT",EDGE,{"derivedFrom":subQ4}),-1.0]])]});}
            var Q1;
            {var subQ4=sQuery(id+"F12.wireOp",EDGE,"E48.MirrorCS");Q1=makeQuery(id+"F12.imprint","IMPRINT",FACE,{"disambiguationData":[TD([[makeQuery(id+"F12.imprint","IMPRINT",EDGE,{"derivedFrom":subQ4}),1.0]])]});}
            extrude(context, id + "F15", {"entities" : qUnion([Q0, Q1]), "operationType" : NewBodyOperationType.ADD, "depth" : .4 * mm, "offsetDistance" : 25 * mm, "hasDraft" : true, "draftAngle" : 3 * degree});
        }
        {
            var Q0;
            {var subQ0=sQuery(id+"F12.wireOp",EDGE,"E48.MirrorCS");Q0=makeQuery(id+"F12.imprint","IMPRINT",FACE,{"disambiguationData":[TD([[makeQuery(id+"F12.imprint","IMPRINT",EDGE,{"derivedFrom":subQ0}),-1.0]])]});}
            var Q1;
            {var subQ0=sQuery(id+"F12.wireOp",EDGE,"E46");Q1=makeQuery(id+"F12.imprint","IMPRINT",FACE,{"disambiguationData":[TD([[makeQuery(id+"F12.imprint","IMPRINT",EDGE,{"derivedFrom":subQ0}),1.0]])]});}
            extrude(context, id + "F16", {"entities" : qUnion([Q0, Q1]), "operationType" : NewBodyOperationType.ADD, "depth" : .5 * mm, "offsetDistance" : 25 * mm});
        }
        {
            var Q0;
            Q0=makeQuery(id+"F12.imprint","IMPRINT",FACE,{"disambiguationData":[TD([[makeQuery(id+"F12.imprint","IMPRINT",EDGE,{"derivedFrom":sQuery(id+"F12.wireOp",EDGE,"E50.2.0")}),-1.0]])]});
            var Q1;
            Q1=makeQuery(id+"F12.imprint","IMPRINT",FACE,{"disambiguationData":[TD([[makeQuery(id+"F12.imprint","IMPRINT",EDGE,{"derivedFrom":sQuery(id+"F12.wireOp",EDGE,"E50.1.0")}),-1.0]])]});
            extrude(context, id + "F17", {"entities" : qUnion([Q0, Q1]), "operationType" : NewBodyOperationType.ADD, "depth" : .2 * mm, "offsetDistance" : 25 * mm});
        }
        {
            var Q0;
            Q0=makeQuery(id+"F12.imprint","IMPRINT",FACE,{"disambiguationData":[TD([[makeQuery(id+"F12.imprint","IMPRINT",EDGE,{"derivedFrom":sQuery(id+"F12.wireOp",EDGE,"E50.1.0")}),1.0]])]});
            var Q1;
            Q1=makeQuery(id+"F12.imprint","IMPRINT",FACE,{"disambiguationData":[TD([[makeQuery(id+"F12.imprint","IMPRINT",EDGE,{"derivedFrom":sQuery(id+"F12.wireOp",EDGE,"E50.2.0")}),1.0]])]});
            extrude(context, id + "F18", {"entities" : qUnion([Q0, Q1]), "operationType" : NewBodyOperationType.ADD, "depth" : .3 * mm, "offsetDistance" : 25 * mm});
        }
        {
            var Q0;
            Q0=makeQuery(id+"F12.imprint","IMPRINT",FACE,{"disambiguationData":[TD([[makeQuery(id+"F12.imprint","IMPRINT",EDGE,{"derivedFrom":sQuery(id+"F12.wireOp",EDGE,"E50.2.2")}),1.0]])]});
            var Q1;
            Q1=makeQuery(id+"F12.imprint","IMPRINT",FACE,{"disambiguationData":[TD([[makeQuery(id+"F12.imprint","IMPRINT",EDGE,{"derivedFrom":sQuery(id+"F12.wireOp",EDGE,"E50.1.2")}),1.0]])]});
            extrude(context, id + "F19", {"entities" : qUnion([Q0, Q1]), "operationType" : NewBodyOperationType.ADD, "depth" : .4 * mm, "offsetDistance" : 25 * mm});
        }
        {
            var Q0;
            Q0=makeQuery(id+"F12.imprint","IMPRINT",FACE,{"disambiguationData":[TD([[makeQuery(id+"F12.imprint","IMPRINT",EDGE,{"derivedFrom":sQuery(id+"F12.wireOp",EDGE,"E50.2.2")}),-1.0]])]});
            var Q1;
            Q1=makeQuery(id+"F12.imprint","IMPRINT",FACE,{"disambiguationData":[TD([[makeQuery(id+"F12.imprint","IMPRINT",EDGE,{"derivedFrom":sQuery(id+"F12.wireOp",EDGE,"E50.1.2")}),-1.0]])]});
            extrude(context, id + "F20", {"entities" : qUnion([Q0, Q1]), "operationType" : NewBodyOperationType.ADD, "depth" : .6 * mm, "offsetDistance" : 25 * mm});
        }
        {
            var Q0;
            Q0=qCreatedBy(makeId("Top.planeOp"),FACE);
            var sketch = newSketch(context, id + "F21", { "sketchPlane" : qUnion([Q0])});
            skCircle(sketch, "E51", {"center": v(-45.22, 35.22) * mm, "radius": 12 * mm});
            skCircle(sketch, "E52", {"center": v(-45.22, 35.22) * mm, "radius": 10.5 * mm});
            skCircle(sketch, "E53", {"center": v(-45.22, 35.22) * mm, "radius": 4 * mm});
            skCircle(sketch, "E54", {"center": v(-55.8, 4.08) * mm, "radius": 12 * mm});
            skCircle(sketch, "E55", {"center": v(-55.8, 4.08) * mm, "radius": 10.5 * mm});
            skCircle(sketch, "E56", {"center": v(-55.8, 4.08) * mm, "radius": 4 * mm});
            skSolve(sketch);
        }
        {
            var Q0;
            Q0 = qSketchRegion(id + "F21", true);
            var Q1;
            Q1=makeQuery(id+"F21.imprint","IMPRINT",FACE,{"disambiguationData":[TD([[makeQuery(id+"F21.imprint","IMPRINT",EDGE,{"derivedFrom":sQuery(id+"F21.wireOp",EDGE,"E52")}),1.0]])]});
            var Q2;
            Q2=makeQuery(id+"F21.imprint","IMPRINT",FACE,{"disambiguationData":[TD([[makeQuery(id+"F21.imprint","IMPRINT",EDGE,{"derivedFrom":sQuery(id+"F21.wireOp",EDGE,"E53")}),1.0]])]});
            var Q3;
            Q3=makeQuery(id+"F21.imprint","IMPRINT",FACE,{"disambiguationData":[TD([[makeQuery(id+"F21.imprint","IMPRINT",EDGE,{"derivedFrom":sQuery(id+"F21.wireOp",EDGE,"E55")}),1.0]])]});
            var Q4;
            Q4=makeQuery(id+"F21.imprint","IMPRINT",FACE,{"disambiguationData":[TD([[makeQuery(id+"F21.imprint","IMPRINT",EDGE,{"derivedFrom":sQuery(id+"F21.wireOp",EDGE,"E56")}),1.0]])]});
            extrude(context, id + "F22", {"entities" : qUnion([Q0, Q1, Q2, Q3, Q4]), "depth" : .5 * mm, "offsetDistance" : 25 * mm});
        }
        {
            var Q0;
            Q0=makeQuery(id+"F21.imprint","IMPRINT",FACE,{"disambiguationData":[TD([[makeQuery(id+"F21.imprint","IMPRINT",EDGE,{"derivedFrom":sQuery(id+"F21.wireOp",EDGE,"E52")}),1.0]])]});
            extrude(context, id + "F23", {"entities" : qUnion([Q0]), "operationType" : NewBodyOperationType.ADD, "depth" : 1.5 * mm, "offsetDistance" : 25 * mm});
        }
        {
            var Q0;
            Q0=makeQuery(id+"F23.boolean.opBoolean","SPLIT",FACE,{"disambiguationData":[TD([makeQuery(id+"F23.opExtrude","SWEPT_FACE",FACE,{"disambiguationData":[OSD([sQuery(id+"F21.wireOp",EDGE,"E53")])]})])],"derivedFrom":makeQuery(id+"F22.opExtrude","CAP_FACE",FACE,{"disambiguationData":[OSD([sQuery(id+"F21.wireOp",EDGE,"E51")])],"isStart":false})});
            extrude(context, id + "F24", {"entities" : qUnion([Q0]), "operationType" : NewBodyOperationType.ADD, "depth" : 2.1 * mm, "offsetDistance" : 25 * mm});
        }
        {
            var Q0;
            Q0=makeQuery(id+"F21.imprint","IMPRINT",FACE,{"disambiguationData":[TD([[makeQuery(id+"F21.imprint","IMPRINT",EDGE,{"derivedFrom":sQuery(id+"F21.wireOp",EDGE,"E55")}),1.0]])]});
            extrude(context, id + "F25", {"entities" : qUnion([Q0]), "operationType" : NewBodyOperationType.ADD, "depth" : 1.5 * mm, "offsetDistance" : 25 * mm});
        }
        {
            var Q0;
            Q0=makeQuery(id+"F21.imprint","IMPRINT",FACE,{"disambiguationData":[TD([[makeQuery(id+"F21.imprint","IMPRINT",EDGE,{"derivedFrom":sQuery(id+"F21.wireOp",EDGE,"E56")}),1.0]])]});
            extrude(context, id + "F26", {"entities" : qUnion([Q0]), "operationType" : NewBodyOperationType.ADD, "depth" : 2.5 * mm, "offsetDistance" : 25 * mm});
        }
    });
